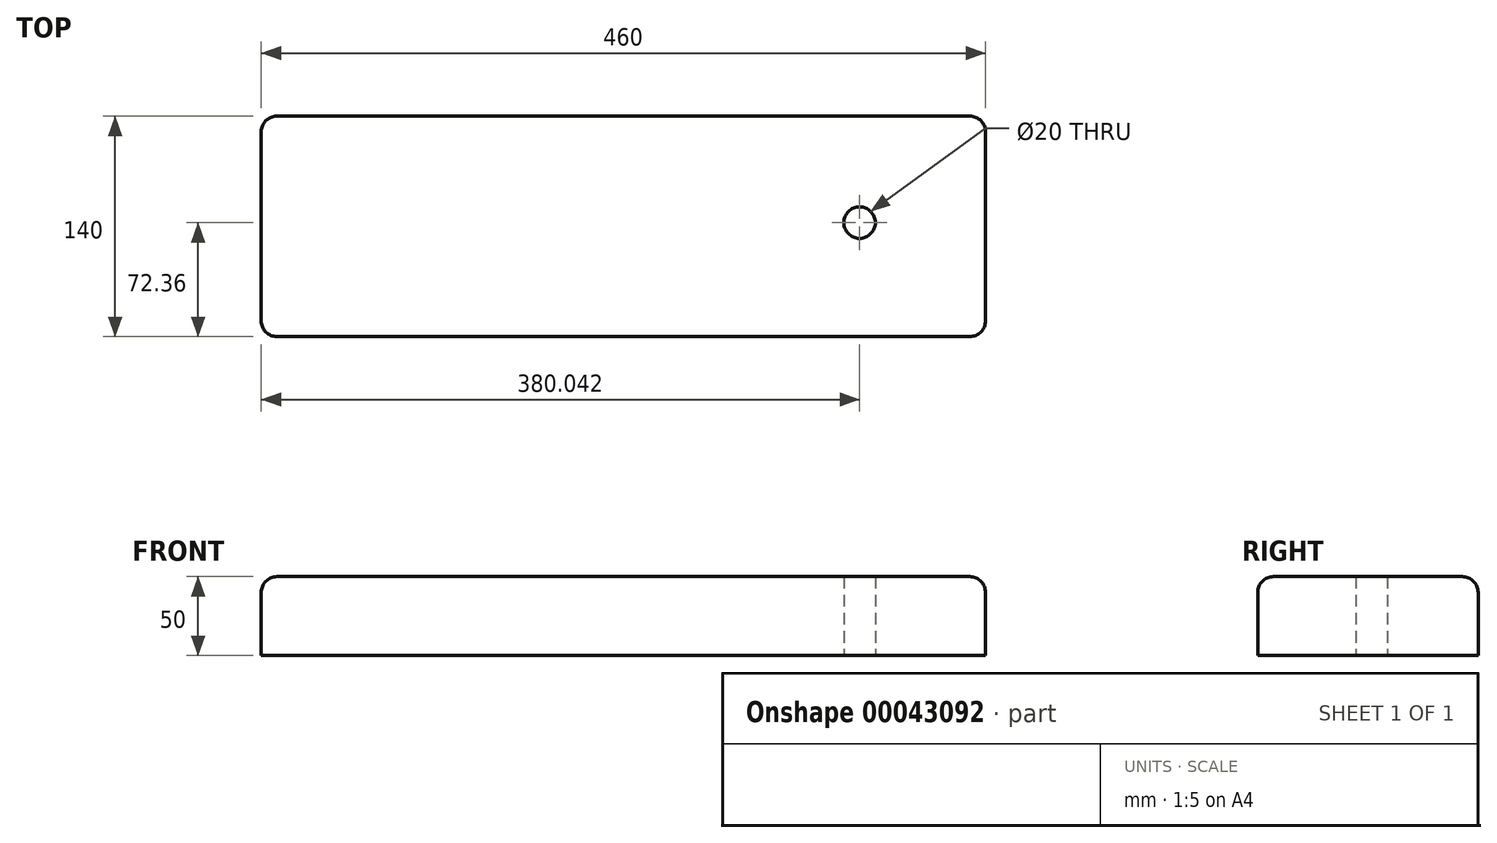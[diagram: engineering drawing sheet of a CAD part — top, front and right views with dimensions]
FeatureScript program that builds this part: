
annotation { "Feature Type Name" : "Feature", "Feature Type Description" : "" }
export const myFeature = defineFeature(function(context is Context, id is Id, definition is map)
    precondition{}
    {
        {
            var Q0;
            Q0=qCreatedBy(makeId("Top.planeOp"),FACE);
            var sketch = newSketch(context, id + "F0", { "sketchPlane" : qUnion([Q0])});
            skLineSegment(sketch, "E0.bottom", {"start": v(-233.7, -72.36) * mm, "end": v(226.3, -72.36) * mm});
            skLineSegment(sketch, "E0.top", {"start": v(-233.7, 67.64) * mm, "end": v(226.3, 67.64) * mm});
            skLineSegment(sketch, "E0.left", {"start": v(-233.7, -72.36) * mm, "end": v(-233.7, 67.64) * mm});
            skLineSegment(sketch, "E0.right", {"start": v(226.3, -72.36) * mm, "end": v(226.3, 67.64) * mm});
            skSolve(sketch);
        }
        {
            var Q0;
            Q0=makeQuery(id+"F0.imprint","IMPRINT",FACE,{"disambiguationData":[TD([[makeQuery(id+"F0.imprint","IMPRINT",EDGE,{"derivedFrom":sQuery(id+"F0.wireOp",EDGE,"E0.bottom")}),1.0]])]});
            extrude(context, id + "F1", {"entities" : qUnion([Q0]), "depth" : 50 * mm});
        }
        {
            var Q0;
            Q0=makeQuery(id+"F1.opExtrude","CAP_FACE",FACE,{"disambiguationData":[OSD([sQuery(id+"F0.wireOp",EDGE,"E0.bottom"),sQuery(id+"F0.wireOp",EDGE,"E0.top"),sQuery(id+"F0.wireOp",EDGE,"E0.left"),sQuery(id+"F0.wireOp",EDGE,"E0.right")])],"isStart":true});
            var sketch = newSketch(context, id + "F2", { "sketchPlane" : qUnion([Q0])});
            skCircle(sketch, "E1", {"center": v(146.34, 0) * mm, "radius": 10 * mm});
            skSolve(sketch);
        }
        {
            var Q0;
            Q0=makeQuery(id+"F2.imprint","IMPRINT",FACE,{"disambiguationData":[TD([[makeQuery(id+"F2.imprint","IMPRINT",EDGE,{"derivedFrom":sQuery(id+"F2.wireOp",EDGE,"E1")}),1.0]])]});
            extrude(context, id + "F3", {"entities" : qUnion([Q0]), "operationType" : NewBodyOperationType.REMOVE, "oppositeDirection" : true, "depth" : 25 * mm});
        }
        {
            var Q0;
            Q0=makeQuery(id+"F3.boolean.opBoolean","COPY",FACE,{"derivedFrom":makeQuery(id+"F3.opExtrude","CAP_FACE",FACE,{"disambiguationData":[OSD([sQuery(id+"F2.wireOp",EDGE,"E1")])],"isStart":false})});
            extrude(context, id + "F4", {"entities" : qUnion([Q0]), "operationType" : NewBodyOperationType.REMOVE, "oppositeDirection" : true, "depth" : 25 * mm});
        }
        {
            var Q0;
            Q0=makeQuery(id+"F1.opExtrude","SWEPT_EDGE",EDGE,{"disambiguationData":[OSD([sQuery(id+"F0.wireOp",EDGE,"E0.bottom"),sQuery(id+"F0.wireOp",EDGE,"E0.left")])]});
            var Q1;
            Q1=makeQuery(id+"F1.opExtrude","CAP_EDGE",EDGE,{"disambiguationData":[OSD([sQuery(id+"F0.wireOp",EDGE,"E0.bottom")])],"isStart":false});
            var Q2;
            Q2=makeQuery(id+"F1.opExtrude","CAP_EDGE",EDGE,{"disambiguationData":[OSD([sQuery(id+"F0.wireOp",EDGE,"E0.left")])],"isStart":false});
            fillet(context, id + "F5", {"entities" : qUnion([Q0, Q1, Q2]), "radius" : 10 * mm, "tangentPropagation" : true, "allowEdgeOverflow" : false});
        }
        {
            var Q0;
            Q0=makeQuery(id+"F1.opExtrude","SWEPT_EDGE",EDGE,{"disambiguationData":[OSD([sQuery(id+"F0.wireOp",EDGE,"E0.bottom"),sQuery(id+"F0.wireOp",EDGE,"E0.right")])]});
            var Q1;
            Q1=makeQuery(id+"F1.opExtrude","SWEPT_EDGE",EDGE,{"disambiguationData":[OSD([sQuery(id+"F0.wireOp",EDGE,"E0.top"),sQuery(id+"F0.wireOp",EDGE,"E0.right")])]});
            var Q2;
            Q2=makeQuery(id+"F1.opExtrude","CAP_EDGE",EDGE,{"disambiguationData":[OSD([sQuery(id+"F0.wireOp",EDGE,"E0.top")])],"isStart":false});
            fillet(context, id + "F6", {"entities" : qUnion([Q0, Q1, Q2]), "radius" : 10 * mm, "tangentPropagation" : true, "allowEdgeOverflow" : false});
        }
    });
